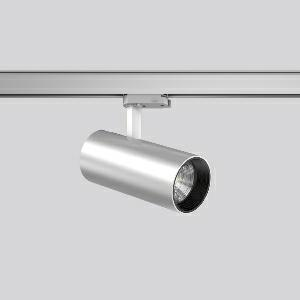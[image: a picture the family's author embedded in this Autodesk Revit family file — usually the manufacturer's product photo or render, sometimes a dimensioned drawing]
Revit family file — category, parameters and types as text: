
# Revit family: deecos_s_mini_742208_004_2_544a
name_source: partatom
category: Lighting Fixtures
units: mm (PartAtom-declared; Revit-internal decimal feet)

## family parameters
Cut with Voids When Loaded = No
Host = Face
Light Source = No
Part Type = Normal
Room Calculation Point = No
Round Connector Dimension = Use Diameter
Shared = No

## types (1)
- DEECOS S mini (1 x LED Modul 927, 2700 lm, 2700)
    Apparent Load = 29 VA
    Approval mark = CE
    CIE Flux Codes = 98 100 100 100 100
    Color Rendering = 92
    Color Temperature = 2700
    Default Elevation = 1800 mm
    Description = Series: DEECOS S mini
LED surface-mounted projector in modern design with no visible cooling ribs. Housing: die-cast aluminium, powder-coated. Rotation range: 356°. Swivel range: 90°. Black plastic ring and recessed LED to prevent glare from the side. Optical assembly with lens made of plastic (polycarbonate) for the best homogeneous light distribution - can be changed without tools. Best colour rendering index Ra>90. With multi adaptor for 3-circuit tracks 230 V. Suitable for Track on ceiling, Wall track. High quality converter without flickering and stroboscopic effect. The following accessories can be mounted without use of tools: interchangeable lenses, decorative glasses, honeycomb louvre, clear and frosted diffusers, white interchangeable plastic ring. 
Colour: silver
Diameter: 87 mm
Height: 214 mm
Lamp: LED
Socket: without socket
Colour temperature: 2700K
Colour rendering index (CRI): 92
System power: 29 W
Rated luminous flux: 2700 lm
Luminous efficiency: 93 lm/W
Control gear: Regulated power supply
Protection class: I
Type of protection: IP 20
    Height = 214 mm
    Lamp = 1 x LED Modul 927
    Lamp Light Flux = 2700 lm
    Lamp count = 1
    Length = 87 mm
    Lifetime = 50000 h
    Luminous efficacy = 93 lm/W
    Manufacturer = RZB
    ModVariant = No
    Model = 742208.004.2
    Mounting Place = Ceiling
    Mounting Type = Rail mounted
    Number of Poles = 1
    OnlyDefault = Yes
    Power Factor = 1
    Product Name = DEECOS S mini
    Product group = Track mounted projectors
    ProductGroupID = 301
    Protection Class = Protection class I
    Protection Degree = IP 20
    RLX_Detail_Level = 1
    RLX_Emergency_Light_Flux = 0 lm
    RLX_Emergency_Type = 0
    RLX_Emergency_Type_DB = No
    RlxData = <blob elided: 37517 chars, md5=ec7eb323>
    Socket = socket
    Standby Power = 0 W
    System Light Flux = 2700 lm
    System Power = 29 W
    Type Comments = Product without accessories
    Type Image = 741930.004.jpg
    URL = http://relux.com
    VarID = ---
    Voltage = 230 V
    Voltage Range = 220-240 V
    Weight = 0.00 kg
    Width = 0 mm  [stored 0 ft]

note: [stored X ft] marks values corroborated as IEEE doubles in the binary element streams (Revit-internal decimal feet)

## geometry (parser evidence)
native form markers: Blend x4, Sweep x12
no freeform markers — native parametric forms only
